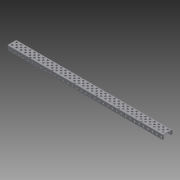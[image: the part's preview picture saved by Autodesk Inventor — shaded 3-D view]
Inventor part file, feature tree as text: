
AUTODESK INVENTOR PART (.ipt)
format: ipt  version: 2015 (Build 190159000, 159)  size: 2,811,392 bytes
history: native  units: in
note: dims shown in document units (in); Inventor stores cm internally (conversion verified against a paired STEP export)
features: other x176, extrude x174, pattern_linear x5, sketch x4, imported_body x1
ambient origin geometry x8: Origin, YZ Plane, XZ Plane, XY Plane, X Axis, Y Axis, Z Axis, Center Point
bodies: Body1 (feature_tree), Body2 (feature_tree), Body3 (feature_tree), Body4 (feature_tree), Body5 (feature_tree), Body6 (feature_tree), Body7 (feature_tree), Body8 (feature_tree), Body9 (feature_tree), Body10 (feature_tree), Body11 (feature_tree), Body12 (feature_tree), Body13 (feature_tree), Body14 (feature_tree), Body15 (feature_tree), Body16 (feature_tree), Body17 (feature_tree), Body18 (feature_tree), Body19 (feature_tree), Body20 (feature_tree), Body21 (feature_tree), Body22 (feature_tree), Body23 (feature_tree), Body24 (feature_tree), Body25 (feature_tree), Body26 (feature_tree), Body27 (feature_tree), Body28 (feature_tree), Body29 (feature_tree), Body30 (feature_tree), Body31 (feature_tree), Body32 (feature_tree), Body33 (feature_tree), Body34 (feature_tree), Body35 (feature_tree), Body36 (feature_tree), Body37 (feature_tree), Body38 (feature_tree), Body39 (feature_tree), Body40 (feature_tree), Body41 (feature_tree), Body42 (feature_tree), Body43 (feature_tree), Body44 (feature_tree), Body45 (feature_tree), Body46 (feature_tree), Body47 (feature_tree), Body48 (feature_tree), Body49 (feature_tree), Body50 (feature_tree), Body51 (feature_tree), Body52 (feature_tree), Body53 (feature_tree), Body54 (feature_tree), Body55 (feature_tree), Body56 (feature_tree), Body57 (feature_tree), Body58 (feature_tree), Body59 (feature_tree), Body60 (feature_tree), Body61 (feature_tree), Body62 (feature_tree), Body63 (feature_tree), Body64 (feature_tree), Body65 (feature_tree), Body66 (feature_tree), Body67 (feature_tree), Body68 (feature_tree), Body69 (feature_tree), Body70 (feature_tree), Body71 (feature_tree), Body72 (feature_tree), Body73 (feature_tree), Body74 (feature_tree), Body75 (feature_tree), Body76 (feature_tree), Body77 (feature_tree), Body78 (feature_tree), Body79 (feature_tree), Body80 (feature_tree), Body81 (feature_tree), Body82 (feature_tree), Body83 (feature_tree), Body84 (feature_tree), Body85 (feature_tree), Body86 (feature_tree), Body87 (feature_tree), Body88 (feature_tree), Body89 (feature_tree), Body90 (feature_tree), Body91 (feature_tree), Body92 (feature_tree), Body93 (feature_tree), Body94 (feature_tree), Body95 (feature_tree), Body96 (feature_tree), Body97 (feature_tree), Body98 (feature_tree), Body99 (feature_tree), Body100 (feature_tree), Body101 (feature_tree), Body102 (feature_tree), Body103 (feature_tree), Body104 (feature_tree), Body105 (feature_tree), Body106 (feature_tree), Body107 (feature_tree), Body108 (feature_tree), Body109 (feature_tree), Body110 (feature_tree), Body111 (feature_tree), Body112 (feature_tree), Body113 (feature_tree), Body114 (feature_tree), Body115 (feature_tree), Body116 (feature_tree), Body117 (feature_tree), Body118 (feature_tree), Body119 (feature_tree), Body120 (feature_tree), Body121 (feature_tree), Body122 (feature_tree), Body123 (feature_tree), Body124 (feature_tree), Body125 (feature_tree), Body126 (feature_tree), Body127 (feature_tree), Body128 (feature_tree), Body129 (feature_tree), Body130 (feature_tree), Body131 (feature_tree), Body132 (feature_tree), Body133 (feature_tree), Body134 (feature_tree), Body135 (feature_tree), Body136 (feature_tree), Body137 (feature_tree), Body138 (feature_tree), Body139 (feature_tree), Body140 (feature_tree), Body141 (feature_tree), Body142 (feature_tree), Body143 (feature_tree), Body144 (feature_tree), Body145 (feature_tree), Body146 (feature_tree), Body147 (feature_tree), Body148 (feature_tree), Body149 (feature_tree), Body150 (feature_tree), Body151 (feature_tree), Body152 (feature_tree), Body153 (feature_tree), Body154 (feature_tree), Body155 (feature_tree), Body156 (feature_tree), Body157 (feature_tree), Body158 (feature_tree), Body159 (feature_tree), Body160 (feature_tree), Body161 (feature_tree), Body162 (feature_tree), Body163 (feature_tree), Body164 (feature_tree), Body165 (feature_tree), Body166 (feature_tree), Body167 (feature_tree), Body168 (feature_tree), Body169 (feature_tree), Body170 (feature_tree), Body171 (feature_tree), Body172 (feature_tree), Body173 (feature_tree), Body174 (feature_tree), Body175 (feature_tree)
feature tree (360):
  parser-record x1  (decoder bookkeeping rows leaked as tree rows — omitted from the tree; the rows remain in map.json)
  other  "VL-CHAN-121-35 RevA1"
  pattern_linear  "Rectangular Pattern1"  Count1=2 Spacing1=0.5in
  pattern_linear  "Rectangular Pattern2"  Count1=35 Spacing1=0.5in
  pattern_linear  "Rectangular Pattern3"  Count1=34 Spacing1=0.5in
  pattern_linear  "Rectangular Pattern4"  Count1=35 Spacing1=0.5in
  pattern_linear  "Rectangular Pattern5"  Spacing1=0.05in  [1 undecoded]
  imported_body  "Base1"
  sketch  "Sketch1"  dims[d0=0.05in d1=0.0in d2=0.7874in d4=0.5in d5=13.7795in d7=0.5in]
  other  "Srf1"
  other  "Srf2"
  other  "Srf4"
  other  "Srf6"
  other  "Srf8"
  other  "Srf10"
  other  "Srf12"
  other  "Srf14"
  other  "Srf16"
  other  "Srf18"
  other  "Srf20"
  other  "Srf22"
  other  "Srf24"
  other  "Srf26"
  other  "Srf28"
  other  "Srf30"
  other  "Srf32"
  other  "Srf34"
  other  "Srf36"
  other  "Srf38"
  other  "Srf40"
  other  "Srf42"
  other  "Srf44"
  other  "Srf46"
  other  "Srf48"
  other  "Srf50"
  other  "Srf52"
  other  "Srf54"
  other  "Srf56"
  other  "Srf58"
  other  "Srf60"
  other  "Srf62"
  other  "Srf64"
  other  "Srf66"
  other  "Srf68"
  other  "Srf70"
  other  "Srf3"
  other  "Srf5"
  other  "Srf7"
  other  "Srf9"
  other  "Srf11"
  other  "Srf13"
  other  "Srf15"
  other  "Srf17"
  other  "Srf19"
  other  "Srf21"
  other  "Srf23"
  other  "Srf25"
  other  "Srf27"
  other  "Srf29"
  other  "Srf31"
  other  "Srf33"
  other  "Srf35"
  other  "Srf37"
  other  "Srf39"
  other  "Srf41"
  other  "Srf43"
  other  "Srf45"
  other  "Srf47"
  other  "Srf49"
  other  "Srf51"
  other  "Srf53"
  other  "Srf55"
  other  "Srf57"
  other  "Srf59"
  other  "Srf61"
  other  "Srf63"
  other  "Srf65"
  other  "Srf67"
  other  "Srf69"
  sketch  "Sketch2"  dims[d8=0.05in d9=0.0in d10=13.3858in d12=0.5in]
  other  "Srf71"
  other  "Srf72"
  other  "Srf73"
  other  "Srf74"
  other  "Srf75"
  other  "Srf76"
  other  "Srf77"
  other  "Srf78"
  other  "Srf79"
  other  "Srf80"
  other  "Srf81"
  other  "Srf82"
  other  "Srf83"
  other  "Srf84"
  other  "Srf85"
  other  "Srf86"
  other  "Srf87"
  other  "Srf88"
  other  "Srf89"
  other  "Srf90"
  other  "Srf91"
  other  "Srf92"
  other  "Srf93"
  other  "Srf94"
  other  "Srf95"
  other  "Srf96"
  other  "Srf97"
  other  "Srf98"
  other  "Srf99"
  other  "Srf100"
  other  "Srf101"
  other  "Srf102"
  other  "Srf103"
  other  "Srf104"
  sketch  "Sketch3"  dims[d13=0.05in d14=0.0in d15=13.7795in d17=0.5in]
  other  "Srf105"
  other  "Srf106"
  other  "Srf107"
  other  "Srf108"
  other  "Srf109"
  other  "Srf110"
  other  "Srf111"
  other  "Srf112"
  other  "Srf113"
  other  "Srf114"
  other  "Srf115"
  other  "Srf116"
  other  "Srf117"
  other  "Srf118"
  other  "Srf119"
  other  "Srf120"
  other  "Srf121"
  other  "Srf122"
  other  "Srf123"
  other  "Srf124"
  other  "Srf125"
  other  "Srf126"
  other  "Srf127"
  other  "Srf128"
  other  "Srf129"
  other  "Srf130"
  other  "Srf131"
  other  "Srf132"
  other  "Srf133"
  other  "Srf134"
  other  "Srf135"
  other  "Srf136"
  other  "Srf137"
  other  "Srf138"
  other  "Srf139"
  sketch  "Sketch4"  dims[d18=0.145in d19=0.05in d20=0.0in d21=13.7795in d23=0.5in d24=0.0in d25=0.0in d26=0.0in d27=0.0in d28=0.0in d29=0.0in d30=0.0in d31=0.0in d32=0.0in d33=0.0in d34=0.0in d35=0.0in d36=0.0in d37=0.0in d38=0.0in d39=0.0in d40=0.0in d41=0.0in d42=0.0in d43=0.0in d44=0.0in d45=0.0in d46=0.0in d47=0.0in d48=0.0in d49=0.0in d50=0.0in d51=0.0in d52=0.0in d53=0.0in d54=0.0in d55=0.0in d56=0.0in d57=0.0in d58=0.0in d59=0.0in d60=0.0in d61=0.0in d62=0.0in d63=0.0in d64=0.0in d65=0.0in d66=0.0in d67=0.0in d68=0.0in d69=0.0in d70=0.0in d71=0.0in d72=0.0in d73=0.0in d74=0.0in d75=0.0in d76=0.0in d77=0.0in d78=0.0in d79=0.0in d80=0.0in d81=0.0in d82=0.0in d83=0.0in d84=0.0in d85=0.0in d86=0.0in d87=0.0in d88=0.0in d89=0.0in d90=0.0in d91=0.0in d92=0.0in d93=0.0in d94=0.0in d95=0.0in d96=0.0in d97=0.0in d98=0.0in d99=0.0in d100=0.0in d101=0.0in d102=0.0in d103=0.0in d104=0.0in d105=0.0in d106=0.0in d107=0.0in d108=0.0in d109=0.0in d110=0.0in d111=0.0in d112=0.0in d113=0.0in d114=0.0in d115=0.0in d116=0.0in d117=0.0in d118=0.0in d119=0.0in d120=0.0in d121=0.0in d122=0.0in d123=0.0in d124=0.0in d125=0.0in d126=0.0in d127=0.0in d128=0.0in d129=0.0in d130=0.0in d131=0.0in d132=0.0in d133=0.0in d134=0.0in d135=0.0in d136=0.0in d137=0.0in d138=0.0in d139=0.0in d140=0.0in d141=0.0in d142=0.0in d143=0.0in d144=0.0in d145=0.0in d146=0.0in d147=0.0in d148=0.0in d149=0.0in d150=0.0in d151=0.0in d152=0.0in d153=0.0in d154=0.0in d155=0.0in d156=0.0in d157=0.0in d158=0.0in d159=0.0in d160=0.0in d161=0.0in d162=0.0in d163=0.0in d164=0.0in d165=0.0in d166=0.0in d167=0.0in d168=0.0in d169=0.0in d170=0.0in d171=0.0in d172=0.0in d173=0.0in d174=0.0in d175=0.0in d176=0.0in d177=0.0in d178=0.0in d179=0.0in d180=0.0in d181=0.0in d182=0.0in d183=0.0in d184=0.0in d185=0.0in d186=0.0in d187=0.0in d188=0.0in d189=0.0in d190=0.0in d191=0.0in d192=0.0in d193=0.0in d194=0.0in d195=0.0in d196=0.0in d197=0.0in d198=0.0in d199=0.0in d200=0.0in d201=0.0in d202=0.0in d203=0.0in d204=0.0in d205=0.0in d206=0.0in d207=0.0in d208=0.0in d209=0.0in d210=0.0in d211=0.0in d212=0.0in d213=0.0in d214=0.0in d215=0.0in d216=0.0in d217=0.0in d218=0.0in d219=0.0in d220=0.0in d221=0.0in d222=0.0in d223=0.0in d224=0.0in d225=0.0in d226=0.0in d227=0.0in d228=0.0in d229=0.0in d230=0.0in d231=0.0in d232=0.0in d233=0.0in d234=0.0in d235=0.0in d236=0.0in d237=0.0in d238=0.0in d239=0.0in d240=0.0in d241=0.0in d242=0.0in d243=0.0in d244=0.0in d245=0.0in d246=0.0in d247=0.0in d248=0.0in d249=0.0in d250=0.0in d251=0.0in d252=0.0in d253=0.0in d254=0.0in d255=0.0in d256=0.0in d257=0.0in d258=0.0in d259=0.0in d260=0.0in d261=0.0in d262=0.0in d263=0.0in d264=0.0in d265=0.0in d266=0.0in d267=0.0in d268=0.0in d269=0.0in d270=0.0in d271=0.0in d272=0.0in d273=0.0in d274=0.0in d275=0.0in d276=0.0in d277=0.0in d278=0.0in d279=0.0in d280=0.0in d281=0.0in d282=0.0in d283=0.0in d284=0.0in d285=0.0in d286=0.0in d287=0.0in d288=0.0in d289=0.0in d290=0.0in d291=0.0in d292=0.0in d293=0.0in d294=0.0in d295=0.0in d296=0.0in d297=0.0in d298=0.0in d299=0.0in d300=0.0in d301=0.0in d302=0.0in d303=0.0in d304=0.0in d305=0.0in d306=0.0in d307=0.0in d308=0.0in d309=0.0in d310=0.0in d311=0.0in d312=0.0in d313=0.0in d314=0.0in d315=0.0in d316=0.0in d317=0.0in d318=0.0in d319=0.0in d320=0.0in d321=0.0in d322=0.0in d323=0.0in d324=0.0in d325=0.0in d326=0.0in d327=0.0in d328=0.0in d329=0.0in d330=0.0in d331=0.0in d332=0.0in d333=0.0in d334=0.0in d335=0.0in d336=0.0in d337=0.0in d338=0.0in d339=0.0in d340=0.0in d341=0.0in d342=0.0in d343=0.0in d344=0.0in d345=0.0in d346=0.0in d347=0.0in d348=0.0in d349=0.0in d350=0.0in d351=0.0in d352=0.0in d353=0.0in d354=0.0in d355=0.0in d356=0.0in d357=0.0in d358=0.0in d359=0.0in d360=0.0in d361=0.0in d362=0.0in d363=0.0in d364=0.0in d365=0.0in d366=0.0in d367=0.0in d368=0.0in d369=0.0in d370=0.0in d371=0.0in]
  other  "Srf140"
  other  "Srf141"
  other  "Srf142"
  other  "Srf143"
  other  "Srf144"
  other  "Srf145"
  other  "Srf146"
  other  "Srf147"
  other  "Srf148"
  other  "Srf149"
  other  "Srf150"
  other  "Srf151"
  other  "Srf152"
  other  "Srf153"
  other  "Srf154"
  other  "Srf155"
  other  "Srf156"
  other  "Srf157"
  other  "Srf158"
  other  "Srf159"
  other  "Srf160"
  other  "Srf161"
  other  "Srf162"
  other  "Srf163"
  other  "Srf164"
  other  "Srf165"
  other  "Srf166"
  other  "Srf167"
  other  "Srf168"
  other  "Srf169"
  other  "Srf170"
  other  "Srf171"
  other  "Srf172"
  other  "Srf173"
  other  "Srf174"
  extrude  "ExtrusionSrf1"  Depth=13.7795in
  extrude  "ExtrusionSrf71"  [1 undecoded]
  extrude  "ExtrusionSrf105"  [1 undecoded]
  extrude  "ExtrusionSrf140"  [1 undecoded]
  extrude  "ExtrusionSrf2"  [1 undecoded]
  extrude  "ExtrusionSrf3"  [1 undecoded]
  extrude  "ExtrusionSrf4"  [1 undecoded]
  extrude  "ExtrusionSrf5"  [1 undecoded]
  extrude  "ExtrusionSrf6"  [1 undecoded]
  extrude  "ExtrusionSrf7"  [1 undecoded]
  extrude  "ExtrusionSrf8"  [1 undecoded]
  extrude  "ExtrusionSrf9"  [1 undecoded]
  extrude  "ExtrusionSrf10"  [1 undecoded]
  extrude  "ExtrusionSrf11"  [1 undecoded]
  extrude  "ExtrusionSrf12"  [1 undecoded]
  extrude  "ExtrusionSrf13"  [1 undecoded]
  extrude  "ExtrusionSrf14"  [1 undecoded]
  extrude  "ExtrusionSrf15"  [1 undecoded]
  extrude  "ExtrusionSrf16"  [1 undecoded]
  extrude  "ExtrusionSrf17"  [1 undecoded]
  extrude  "ExtrusionSrf18"  [1 undecoded]
  extrude  "ExtrusionSrf19"  [1 undecoded]
  extrude  "ExtrusionSrf20"  [1 undecoded]
  extrude  "ExtrusionSrf21"  [1 undecoded]
  extrude  "ExtrusionSrf22"  [1 undecoded]
  extrude  "ExtrusionSrf23"  [1 undecoded]
  extrude  "ExtrusionSrf24"  [1 undecoded]
  extrude  "ExtrusionSrf25"  [1 undecoded]
  extrude  "ExtrusionSrf26"  [1 undecoded]
  extrude  "ExtrusionSrf27"  [1 undecoded]
  extrude  "ExtrusionSrf28"  [1 undecoded]
  extrude  "ExtrusionSrf29"  [1 undecoded]
  extrude  "ExtrusionSrf30"  [1 undecoded]
  extrude  "ExtrusionSrf31"  [1 undecoded]
  extrude  "ExtrusionSrf32"  [1 undecoded]
  extrude  "ExtrusionSrf33"  [1 undecoded]
  extrude  "ExtrusionSrf34"  [1 undecoded]
  extrude  "ExtrusionSrf35"  [1 undecoded]
  extrude  "ExtrusionSrf36"  [1 undecoded]
  extrude  "ExtrusionSrf37"  [1 undecoded]
  extrude  "ExtrusionSrf38"  [1 undecoded]
  extrude  "ExtrusionSrf39"  [1 undecoded]
  extrude  "ExtrusionSrf40"  [1 undecoded]
  extrude  "ExtrusionSrf41"  [1 undecoded]
  extrude  "ExtrusionSrf42"  [1 undecoded]
  extrude  "ExtrusionSrf43"  [1 undecoded]
  extrude  "ExtrusionSrf44"  [1 undecoded]
  extrude  "ExtrusionSrf45"  [1 undecoded]
  extrude  "ExtrusionSrf46"  [1 undecoded]
  extrude  "ExtrusionSrf47"  [1 undecoded]
  extrude  "ExtrusionSrf48"  [1 undecoded]
  extrude  "ExtrusionSrf49"  [1 undecoded]
  extrude  "ExtrusionSrf50"  [1 undecoded]
  extrude  "ExtrusionSrf51"  [1 undecoded]
  extrude  "ExtrusionSrf52"  [1 undecoded]
  extrude  "ExtrusionSrf53"  [1 undecoded]
  extrude  "ExtrusionSrf54"  [1 undecoded]
  extrude  "ExtrusionSrf55"  [1 undecoded]
  extrude  "ExtrusionSrf56"  [1 undecoded]
  extrude  "ExtrusionSrf57"  [1 undecoded]
  extrude  "ExtrusionSrf58"  [1 undecoded]
  extrude  "ExtrusionSrf59"  [1 undecoded]
  extrude  "ExtrusionSrf60"  [1 undecoded]
  extrude  "ExtrusionSrf61"  [1 undecoded]
  extrude  "ExtrusionSrf62"  [1 undecoded]
  extrude  "ExtrusionSrf63"  [1 undecoded]
  extrude  "ExtrusionSrf64"  [1 undecoded]
  extrude  "ExtrusionSrf65"  [1 undecoded]
  extrude  "ExtrusionSrf66"  [1 undecoded]
  extrude  "ExtrusionSrf67"  [1 undecoded]
  extrude  "ExtrusionSrf68"  [1 undecoded]
  extrude  "ExtrusionSrf69"  [1 undecoded]
  extrude  "ExtrusionSrf70"  [1 undecoded]
  extrude  "ExtrusionSrf72"  [1 undecoded]
  extrude  "ExtrusionSrf73"  [1 undecoded]
  extrude  "ExtrusionSrf74"  [1 undecoded]
  extrude  "ExtrusionSrf75"  [1 undecoded]
  extrude  "ExtrusionSrf76"  [1 undecoded]
  extrude  "ExtrusionSrf77"  [1 undecoded]
  extrude  "ExtrusionSrf78"  [1 undecoded]
  extrude  "ExtrusionSrf79"  [1 undecoded]
  extrude  "ExtrusionSrf80"  [1 undecoded]
  extrude  "ExtrusionSrf81"  [1 undecoded]
  extrude  "ExtrusionSrf82"  [1 undecoded]
  extrude  "ExtrusionSrf83"  [1 undecoded]
  extrude  "ExtrusionSrf84"  [1 undecoded]
  extrude  "ExtrusionSrf85"  [1 undecoded]
  extrude  "ExtrusionSrf86"  [1 undecoded]
  extrude  "ExtrusionSrf87"  [1 undecoded]
  extrude  "ExtrusionSrf88"  [1 undecoded]
  extrude  "ExtrusionSrf89"  [1 undecoded]
  extrude  "ExtrusionSrf90"  [1 undecoded]
  extrude  "ExtrusionSrf91"  [1 undecoded]
  extrude  "ExtrusionSrf92"  [1 undecoded]
  extrude  "ExtrusionSrf93"  [1 undecoded]
  extrude  "ExtrusionSrf94"  [1 undecoded]
  extrude  "ExtrusionSrf95"  [1 undecoded]
  extrude  "ExtrusionSrf96"  [1 undecoded]
  extrude  "ExtrusionSrf97"  [1 undecoded]
  extrude  "ExtrusionSrf98"  [1 undecoded]
  extrude  "ExtrusionSrf99"  [1 undecoded]
  extrude  "ExtrusionSrf100"  [1 undecoded]
  extrude  "ExtrusionSrf101"  [1 undecoded]
  extrude  "ExtrusionSrf102"  [1 undecoded]
  extrude  "ExtrusionSrf103"  [1 undecoded]
  extrude  "ExtrusionSrf104"  [1 undecoded]
  extrude  "ExtrusionSrf106"  [1 undecoded]
  extrude  "ExtrusionSrf107"  [1 undecoded]
  extrude  "ExtrusionSrf108"  [1 undecoded]
  extrude  "ExtrusionSrf109"  [1 undecoded]
  extrude  "ExtrusionSrf110"  [1 undecoded]
  extrude  "ExtrusionSrf111"  [1 undecoded]
  extrude  "ExtrusionSrf112"  [1 undecoded]
  extrude  "ExtrusionSrf113"  [1 undecoded]
  extrude  "ExtrusionSrf114"  [1 undecoded]
  extrude  "ExtrusionSrf115"  [1 undecoded]
  extrude  "ExtrusionSrf116"  [1 undecoded]
  extrude  "ExtrusionSrf117"  [1 undecoded]
  extrude  "ExtrusionSrf118"  [1 undecoded]
  extrude  "ExtrusionSrf119"  [1 undecoded]
  extrude  "ExtrusionSrf120"  [1 undecoded]
  extrude  "ExtrusionSrf121"  [1 undecoded]
  extrude  "ExtrusionSrf122"  [1 undecoded]
  extrude  "ExtrusionSrf123"  [1 undecoded]
  extrude  "ExtrusionSrf124"  [1 undecoded]
  extrude  "ExtrusionSrf125"  [1 undecoded]
  extrude  "ExtrusionSrf126"  [1 undecoded]
  extrude  "ExtrusionSrf127"  [1 undecoded]
  extrude  "ExtrusionSrf128"  [1 undecoded]
  extrude  "ExtrusionSrf129"  [1 undecoded]
  extrude  "ExtrusionSrf130"  [1 undecoded]
  extrude  "ExtrusionSrf131"  [1 undecoded]
  extrude  "ExtrusionSrf132"  [1 undecoded]
  extrude  "ExtrusionSrf133"  [1 undecoded]
  extrude  "ExtrusionSrf134"  [1 undecoded]
  extrude  "ExtrusionSrf135"  [1 undecoded]
  extrude  "ExtrusionSrf136"  [1 undecoded]
  extrude  "ExtrusionSrf137"  [1 undecoded]
  extrude  "ExtrusionSrf138"  [1 undecoded]
  extrude  "ExtrusionSrf139"  [1 undecoded]
  extrude  "ExtrusionSrf141"  [1 undecoded]
  extrude  "ExtrusionSrf142"  [1 undecoded]
  extrude  "ExtrusionSrf143"  [1 undecoded]
  extrude  "ExtrusionSrf144"  [1 undecoded]
  extrude  "ExtrusionSrf145"  [1 undecoded]
  extrude  "ExtrusionSrf146"  [1 undecoded]
  extrude  "ExtrusionSrf147"  [1 undecoded]
  extrude  "ExtrusionSrf148"  [1 undecoded]
  extrude  "ExtrusionSrf149"  [1 undecoded]
  extrude  "ExtrusionSrf150"  [1 undecoded]
  extrude  "ExtrusionSrf151"  [1 undecoded]
  extrude  "ExtrusionSrf152"  [1 undecoded]
  extrude  "ExtrusionSrf153"  [1 undecoded]
  extrude  "ExtrusionSrf154"  [1 undecoded]
  extrude  "ExtrusionSrf155"  [1 undecoded]
  extrude  "ExtrusionSrf156"  [1 undecoded]
  extrude  "ExtrusionSrf157"  [1 undecoded]
  extrude  "ExtrusionSrf158"  [1 undecoded]
  extrude  "ExtrusionSrf159"  [1 undecoded]
  extrude  "ExtrusionSrf160"  [1 undecoded]
  extrude  "ExtrusionSrf161"  [1 undecoded]
  extrude  "ExtrusionSrf162"  [1 undecoded]
  extrude  "ExtrusionSrf163"  [1 undecoded]
  extrude  "ExtrusionSrf164"  [1 undecoded]
  extrude  "ExtrusionSrf165"  [1 undecoded]
  extrude  "ExtrusionSrf166"  [1 undecoded]
  extrude  "ExtrusionSrf167"  [1 undecoded]
  extrude  "ExtrusionSrf168"  [1 undecoded]
  extrude  "ExtrusionSrf169"  [1 undecoded]
  extrude  "ExtrusionSrf170"  [1 undecoded]
  extrude  "ExtrusionSrf171"  [1 undecoded]
  extrude  "ExtrusionSrf172"  [1 undecoded]
  extrude  "ExtrusionSrf173"  [1 undecoded]
  extrude  "ExtrusionSrf174"  [1 undecoded]
note: 174 required parameter values undecoded (feature->parameter linkage not recoverable at this tier; creation-order binding heuristic only, values carry confidence <= 0.55)
